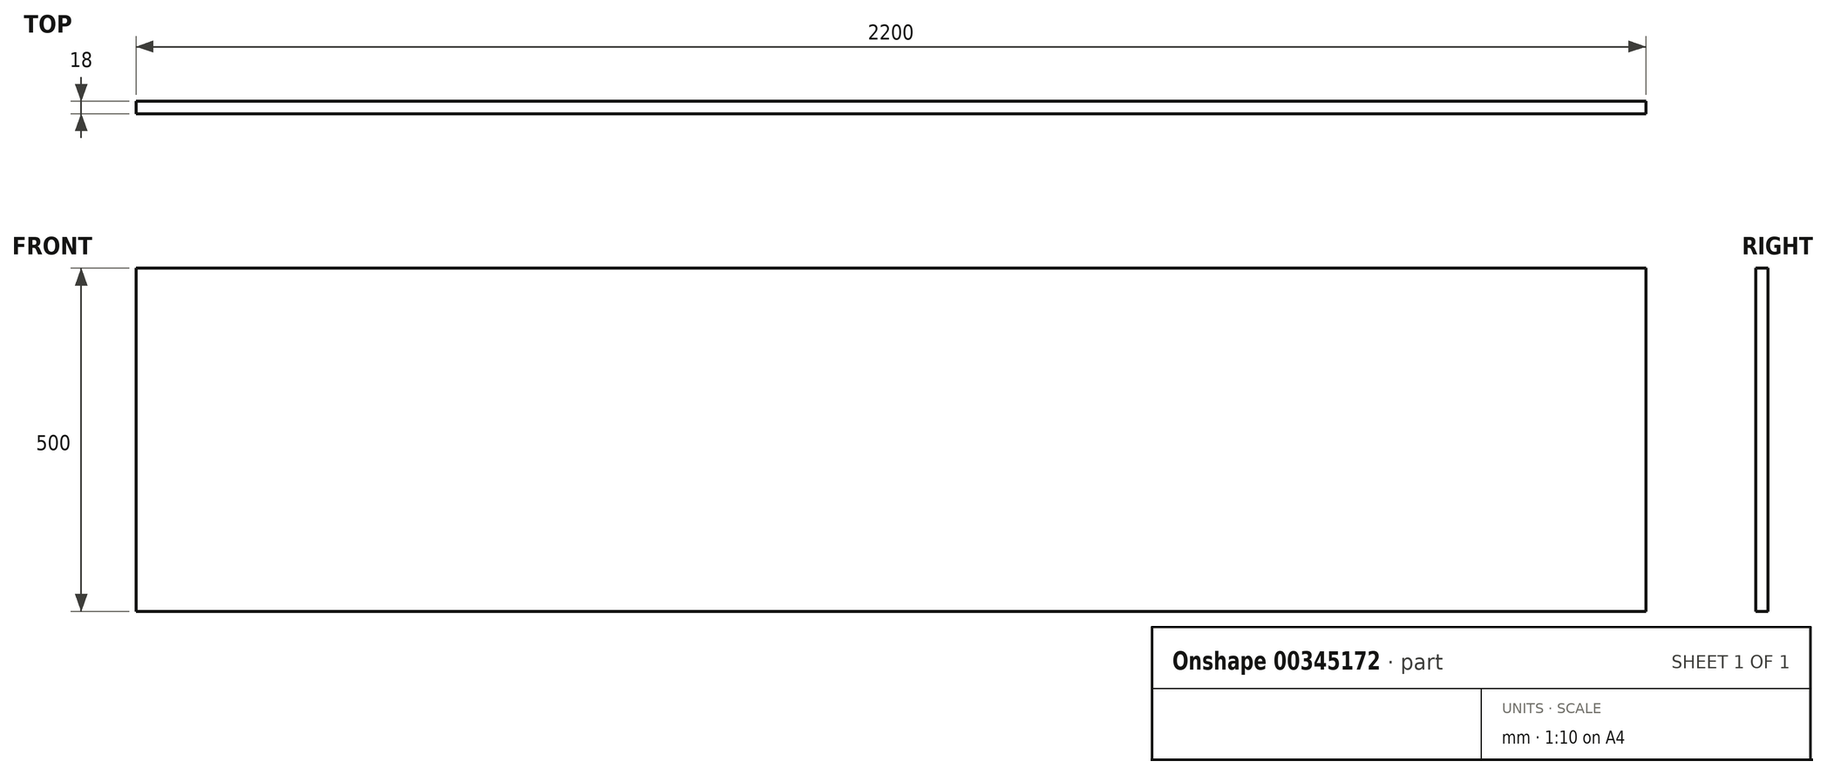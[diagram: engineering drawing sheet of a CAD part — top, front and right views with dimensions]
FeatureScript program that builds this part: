
annotation { "Feature Type Name" : "Feature", "Feature Type Description" : "" }
export const myFeature = defineFeature(function(context is Context, id is Id, definition is map)
    precondition{}
    {
        {
            var Q0;
            Q0=qCreatedBy(makeId("Front.planeOp"),FACE);
            var sketch = newSketch(context, id + "F0", { "sketchPlane" : qUnion([Q0])});
            skLineSegment(sketch, "E0.bottom", {"start": v(0, 0) * mm, "end": v(-43.5, 0) * mm});
            skLineSegment(sketch, "E0.top", {"start": v(0, 32.22) * mm, "end": v(-43.5, 32.22) * mm});
            skLineSegment(sketch, "E0.left", {"start": v(0, 0) * mm, "end": v(0, 32.22) * mm});
            skLineSegment(sketch, "E0.right", {"start": v(-43.5, 0) * mm, "end": v(-43.5, 32.22) * mm});
            skSolve(sketch);
        }
        {
            var Q0;
            Q0=makeQuery(id+"F0.imprint","IMPRINT",FACE,{"disambiguationData":[TD([[makeQuery(id+"F0.imprint","IMPRINT",EDGE,{"derivedFrom":sQuery(id+"F0.wireOp",EDGE,"E0.bottom")}),-1.0]])]});
            extrude(context, id + "F1", {"entities" : qUnion([Q0]), "oppositeDirection" : true, "depth" : 18 * mm});
        }
        {
            var Q0;
            Q0=makeQuery(id+"F1.opExtrude","SWEPT_FACE",FACE,{"disambiguationData":[OSD([sQuery(id+"F0.wireOp",EDGE,"E0.left")])]});
            extrude(context, id + "F2", {"entities" : qUnion([Q0]), "operationType" : NewBodyOperationType.ADD, "oppositeDirection" : true, "depth" : 2200 * mm});
        }
        {
            var Q0;
            {var subQ0=sQuery(id+"F0.wireOp",EDGE,"E0.bottom");Q0=makeQuery(id+"F2.boolean.opBoolean","MERGE",FACE,{"derivedFrom":[makeQuery(id+"F1.opExtrude","SWEPT_FACE",FACE,{"disambiguationData":[OSD([subQ0])]}),makeQuery(id+"F2.opExtrude","SWEPT_FACE",FACE,{"disambiguationData":[OSD([subQ0,sQuery(id+"F0.wireOp",EDGE,"E0.left")])]})]});}
            extrude(context, id + "F3", {"entities" : qUnion([Q0]), "operationType" : NewBodyOperationType.ADD, "oppositeDirection" : true, "depth" : 500 * mm});
        }
    });
